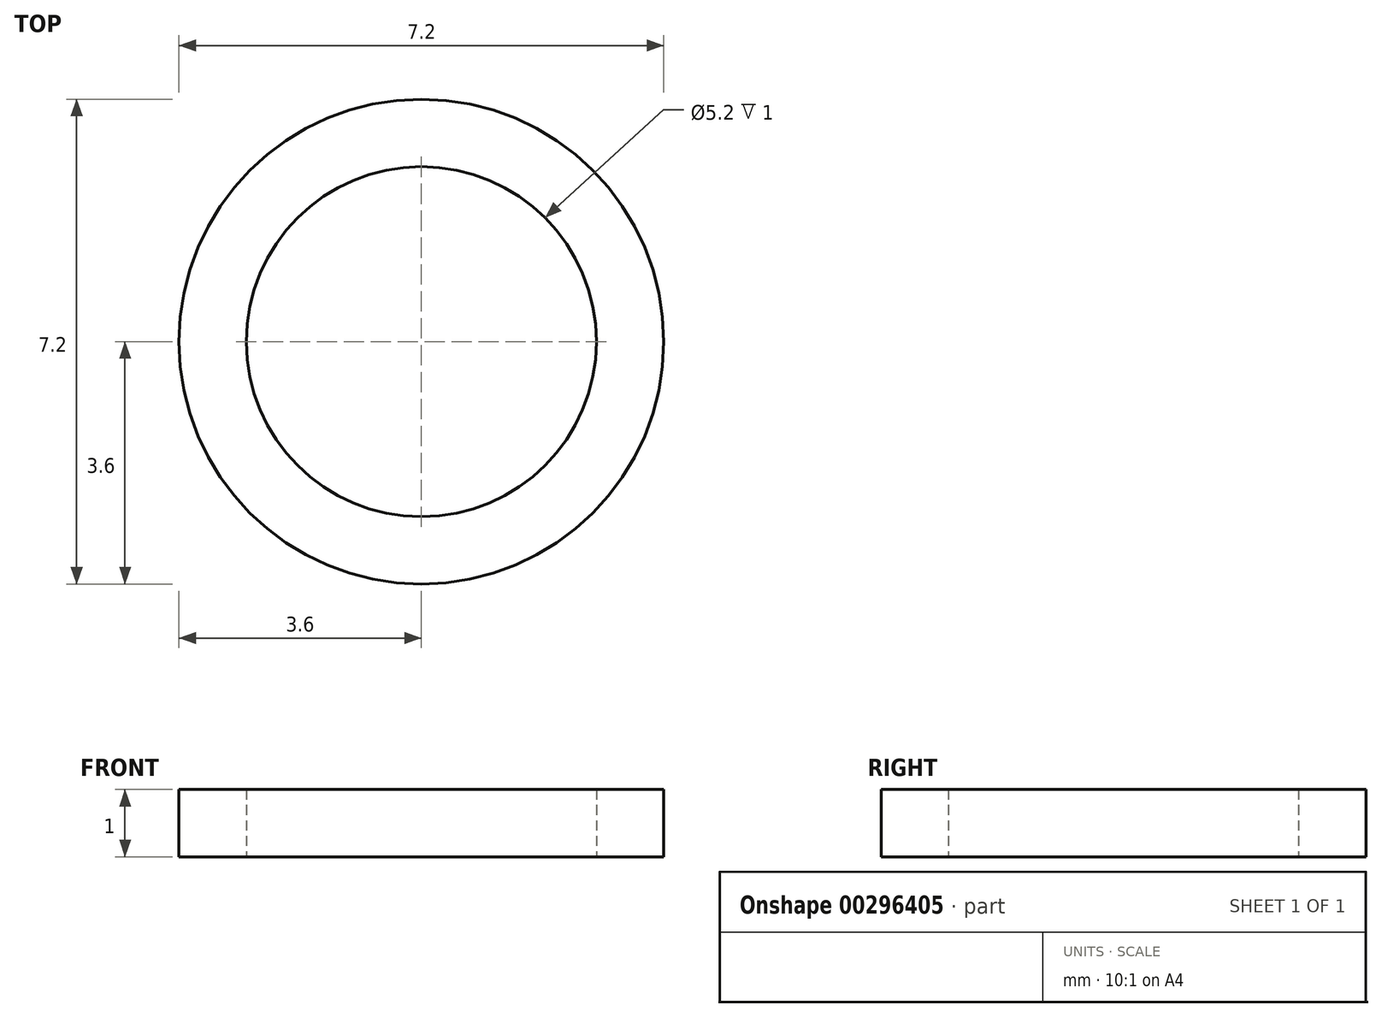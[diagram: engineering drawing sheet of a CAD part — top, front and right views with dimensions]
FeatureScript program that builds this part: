
annotation { "Feature Type Name" : "Feature", "Feature Type Description" : "" }
export const myFeature = defineFeature(function(context is Context, id is Id, definition is map)
    precondition{}
    {
        {
            var Q0;
            Q0=qCreatedBy(makeId("Top.planeOp"),FACE);
            var sketch = newSketch(context, id + "F0", { "sketchPlane" : qUnion([Q0])});
            skCircle(sketch, "E0", {"center": v(0, 0) * mm, "radius": 2.6 * mm});
            skCircle(sketch, "E1", {"center": v(0, 0) * mm, "radius": 3.6 * mm});
            skSolve(sketch);
        }
        {
            var Q0;
            Q0 = qSketchRegion(id + "F0", true);
            extrude(context, id + "F1", {"entities" : qUnion([Q0]), "depth" : 1 * mm, "offsetDistance" : 25 * mm});
        }
    });
